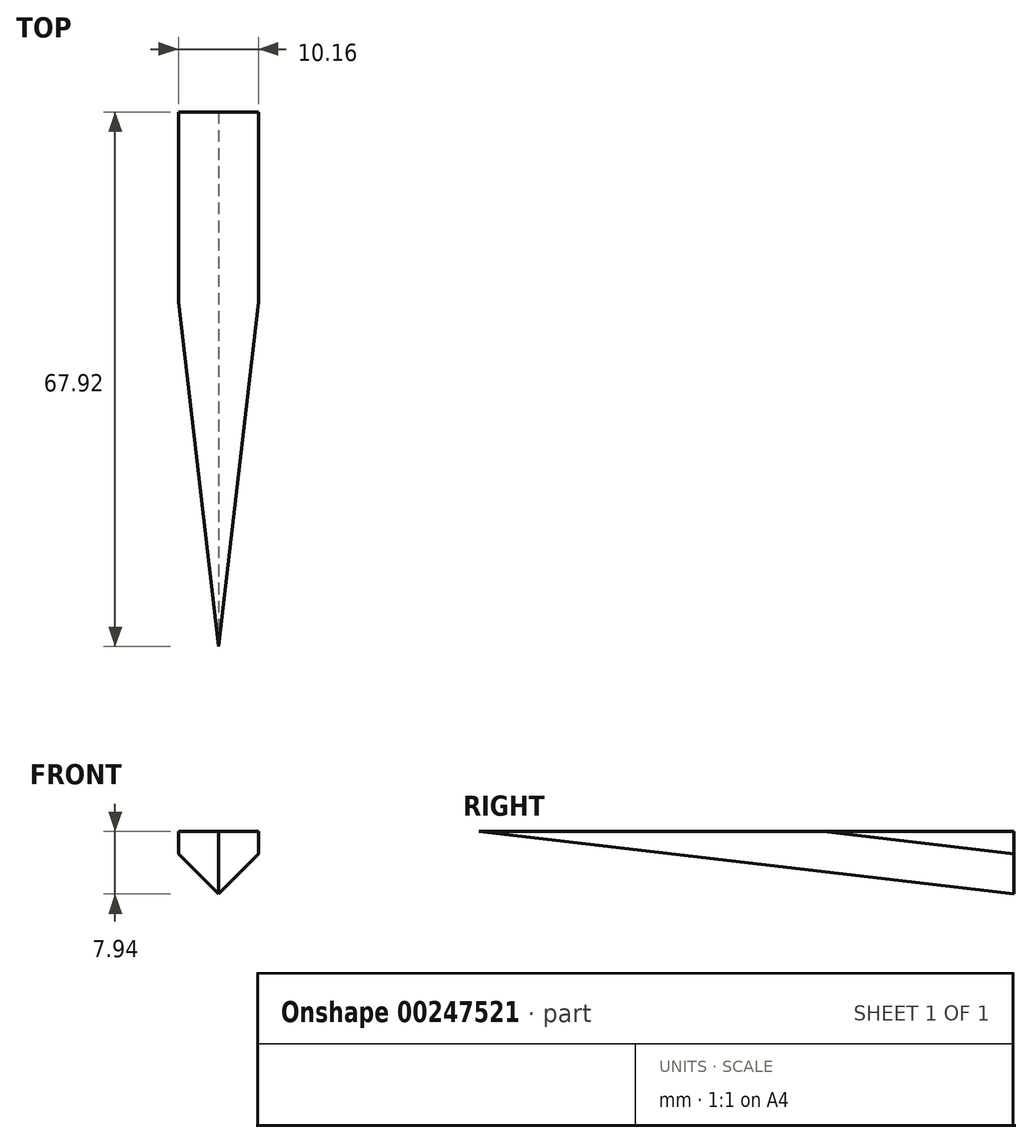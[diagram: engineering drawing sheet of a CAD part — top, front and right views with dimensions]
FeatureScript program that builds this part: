
annotation { "Feature Type Name" : "Feature", "Feature Type Description" : "" }
export const myFeature = defineFeature(function(context is Context, id is Id, definition is map)
    precondition{}
    {
        {
            var Q0;
            Q0=qCreatedBy(makeId("Right.planeOp"),FACE);
            var sketch = newSketch(context, id + "F0", { "sketchPlane" : qUnion([Q0])});
            skLineSegment(sketch, "E0", {"start": v(22.23, -7.94) * mm, "end": v(-45.69, 0) * mm});
            skLineSegment(sketch, "E1", {"start": v(-45.69, 0) * mm, "end": v(22.23, 0) * mm});
            skLineSegment(sketch, "E2", {"start": v(22.23, 0) * mm, "end": v(22.23, -7.94) * mm});
            skSolve(sketch);
        }
        {
            var Q0;
            Q0 = qSketchRegion(id + "F0", true);
            extrude(context, id + "F1", {"entities" : qUnion([Q0]), "depth" : 10.16 * mm});
        }
        {
            var Q0;
            Q0=makeQuery(id+"F1.opExtrude","CAP_EDGE",EDGE,{"disambiguationData":[OSD([sQuery(id+"F0.wireOp",EDGE,"E0")])],"isStart":false});
            var Q1;
            Q1=makeQuery(id+"F1.opExtrude","CAP_EDGE",EDGE,{"disambiguationData":[OSD([sQuery(id+"F0.wireOp",EDGE,"E0")])],"isStart":true});
            chamfer(context, id + "F2", {"entities" : qUnion([Q0, Q1]), "width" : 5.08 * mm, "tangentPropagation" : true});
        }
    });
